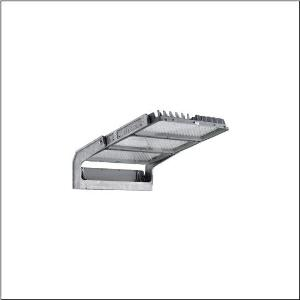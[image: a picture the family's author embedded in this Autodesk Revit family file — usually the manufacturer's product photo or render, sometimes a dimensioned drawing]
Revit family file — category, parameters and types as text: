
# Revit family: floodlight_fl_11_maxi_pro___rs07_5xa779124k02fb_0e28
name_source: partatom
category: Lighting Fixtures
units: mm (PartAtom-declared; Revit-internal decimal feet)

## family parameters
Cut with Voids When Loaded = No
Host = Face
Light Source = No
Part Type = Normal
Room Calculation Point = No
Round Connector Dimension = Use Diameter
Shared = No

## types (1)
- --- (1 x LED, 130880 lm, 1323.9 W, 5700K)
    Apparent Load = 1324 VA
    CIE Flux Codes = 80 93 99 100 99
    Color Rendering = 90
    Color Temperature = 5700K
    Default Elevation = 1800 mm
    Description = Floodlight FL 11  maxi  pro floodlight; light control with lens of PMMA; cover panel of toughened safety glass, transparent; light distribution: RS07, rotationally symmetric direct distribution, LED; colour temperature: 5700K, rated luminous flux: 130.880lm, colour rendering: CRI > 90, light colour: 957; luminous efficacy: 99lm/W; brightness control: DALI 2; with terminal, 5-pole, max. 2.5mm², mains connection: 220..240V/380..400V AC, 50/60Hz, surge voltage resistance: line to ground: 10kV, LED service life up to 100,000h L90. Typical operating time: 1000h per year., ECG replaceable separately, LED unit replaceable without ESD environment, dustproof LED module, dimming range 10..100%; 1324W floodlight with 3x LED unit of diecast aluminium, coated grey; length: 1.003mm / width: 651mm / height: 338mm; mounting bracket, of diecast aluminium, uncoated, natural, equipment: Power, protection rating (complete): IP66; insulation class (complete): insulation class I (protective earthing); certification: CE, ENEC, VDE; ball protection: ball impact resistant, only for outdoor installations in the designated locations, permissible operating ambient temperature: -45..+55°C, permissible storage temperature: -40..+85°Cpackaging unit: 1 piece

Light Distribution: RS07
    Height = 320 mm
    Lamp = 1 x LED
    Lamp Light Flux = 130880 lm
    Lamp Power = 1323.9 W
    Lamp count = 1
    Length = 1002 mm
    Luminous efficacy = 99 lm/W
    Manufacturer = Siteco
    ModVariant = No
    Model = 5XA779124K02FB
    Mounting Place = Ceiling
    Mounting Type = Surface mounted
    Number of Poles = 1
    OnlyDefault = Yes
    Power Factor = 1
    Product Name = Floodlight FL 11 maxi pro | RS07
    Product group = floodlight | ceiling mounted
    ProductGroupID = 303
    Protection Class = Protection class I
    Protection Degree = IP 66
    RLX_Detail_Level = 1
    RLX_Emergency_Light_Flux = 0 lm
    RLX_Emergency_Type = 0
    RLX_Emergency_Type_DB = No
    RlxData = <blob elided: 40101 chars, md5=4325bc01>
    Socket = socket
    Standby Power = 0 W
    System Light Flux = 130880 lm
    System Power = 1324 W
    Type Comments = factory setting: luminous flux: 100 % | dim-lin: 254 | 900 mA
    Type Image = l_1356210.jpg
    URL = http://relux.com
    VarID = @adj_038759
    Voltage = 0 V
    Weight = 0.00 kg
    Width = 655 mm

## geometry (parser evidence)
native form markers: Blend x4, Sweep x10
no freeform markers — native parametric forms only
